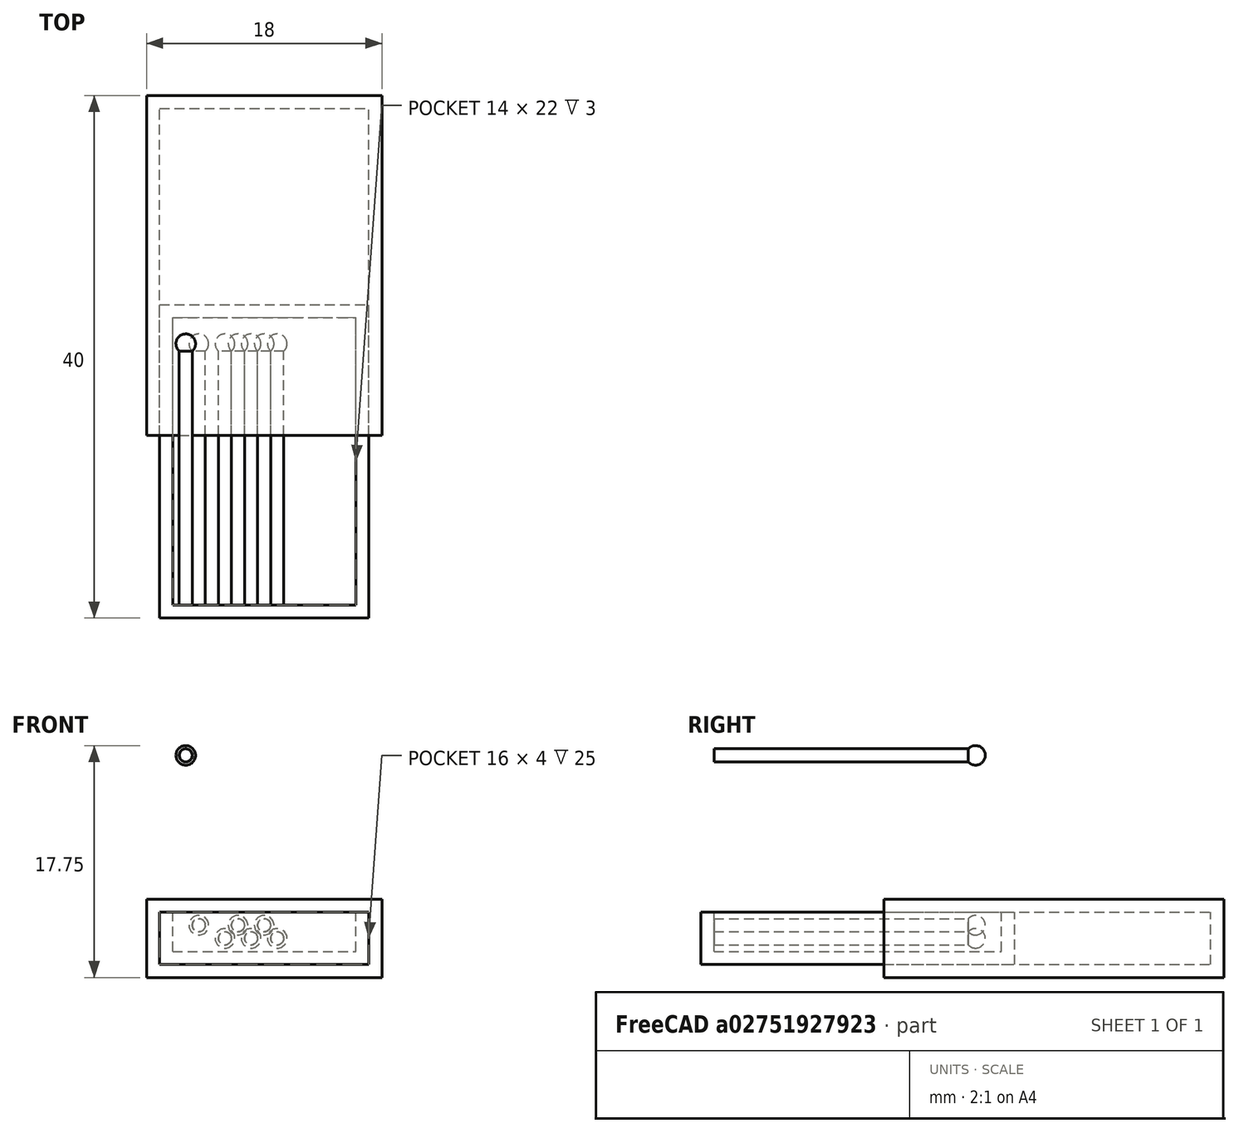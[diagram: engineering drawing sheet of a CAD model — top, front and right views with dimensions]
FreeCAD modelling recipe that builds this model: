
FCSTD DOCUMENT  (FreeCAD 0.18R4 (GitTag))
Label: 1
License: All rights reserved
LicenseURL: http://en.wikipedia.org/wiki/All_rights_reserved
objects: Part::Cylinder×7, Part::Sphere×7, Part::Fuse×7, Part::Box×4, Part::Cut×2
note: 27 computed .brp shape members not serialized (recipe doc carries the construction recipe); baked Part::Feature solids carry a one-line shape summary decoded from their .brp

FEATURE [Part::Box] Box  label="Куб"
  AttacherType = Attacher::AttachEngine3D
  Height = 4
  Length = 16
  Width = 24
FEATURE [Part::Box] Box001  label="Куб001"
  AttacherType = Attacher::AttachEngine3D
  Height = 3
  Length = 14
  Placement = pos=(1,1,1) rot=(0,0,1;0rad)
  Width = 22
FEATURE [Part::Cut] Cut
  Base = -> Box
  Tool = -> Box001
FEATURE [Part::Box] Box002  label="Куб002"
  AttacherType = Attacher::AttachEngine3D
  Height = 6
  Length = 18
  Placement = pos=(-20,2,-1) rot=(0,0,1;0rad)
  Width = 26
FEATURE [Part::Box] Box003  label="Куб003"
  AttacherType = Attacher::AttachEngine3D
  Height = 4
  Length = 16
  Placement = pos=(-19,2,0) rot=(0,0,1;0rad)
  Width = 25
FEATURE [Part::Cut] Cut001
  Base = -> Box002
  Placement = pos=(19,12,0) rot=(0,0,1;0rad)
  Tool = -> Box003
FEATURE [Part::Cylinder] Cylinder  label="Цилиндр"
  Angle = 360
  AttacherType = Attacher::AttachEngine3D
  Height = 20
  Placement = pos=(-13,1,2e-16) rot=(1,0,0;4.71239rad)
  Radius = 0.5
FEATURE [Part::Sphere] Sphere  label="Сфера"
  Angle1 = -90
  Angle2 = 90
  Angle3 = 360
  AttacherType = Attacher::AttachEngine3D
  Placement = pos=(-13,21,0) rot=(0,0,1;0rad)
  Radius = 0.75
FEATURE [Part::Fuse] Fusion
  Base = -> Cylinder
  Placement = pos=(15,0,16) rot=(0,0,1;0rad)
  Tool = -> Sphere
FEATURE [Part::Cylinder] Cylinder001  label="Цилиндр001"
  Angle = 360
  AttacherType = Attacher::AttachEngine3D
  Height = 20
  Placement = pos=(-13,1,0) rot=(-1,0,0;1.5708rad)
  Radius = 0.5
FEATURE [Part::Sphere] Sphere001  label="Сфера001"
  Angle1 = -90
  Angle2 = 90
  Angle3 = 360
  AttacherType = Attacher::AttachEngine3D
  Placement = pos=(-13,21,0) rot=(0,0,1;0rad)
  Radius = 0.75
FEATURE [Part::Fuse] Fusion001
  Base = -> Cylinder001
  Placement = pos=(16,0,3) rot=(0,0,1;0rad)
  Tool = -> Sphere001
FEATURE [Part::Cylinder] Cylinder002  label="Цилиндр002"
  Angle = 360
  AttacherType = Attacher::AttachEngine3D
  Height = 20
  Placement = pos=(-13,1,0) rot=(-1,0,0;1.5708rad)
  Radius = 0.5
FEATURE [Part::Sphere] Sphere002  label="Сфера002"
  Angle1 = -90
  Angle2 = 90
  Angle3 = 360
  AttacherType = Attacher::AttachEngine3D
  Placement = pos=(-13,21,0) rot=(0,0,1;0rad)
  Radius = 0.75
FEATURE [Part::Fuse] Fusion002
  Base = -> Cylinder002
  Placement = pos=(18,0,2) rot=(0,0,1;0rad)
  Tool = -> Sphere002
FEATURE [Part::Cylinder] Cylinder003  label="Цилиндр003"
  Angle = 360
  AttacherType = Attacher::AttachEngine3D
  Height = 20
  Placement = pos=(-13,1,0) rot=(-1,0,0;1.5708rad)
  Radius = 0.5
FEATURE [Part::Sphere] Sphere003  label="Сфера003"
  Angle1 = -90
  Angle2 = 90
  Angle3 = 360
  AttacherType = Attacher::AttachEngine3D
  Placement = pos=(-13,21,0) rot=(0,0,1;0rad)
  Radius = 0.75
FEATURE [Part::Fuse] Fusion003
  Base = -> Cylinder003
  Placement = pos=(19,0,3) rot=(0,0,1;0rad)
  Tool = -> Sphere003
FEATURE [Part::Cylinder] Cylinder004  label="Цилиндр004"
  Angle = 360
  AttacherType = Attacher::AttachEngine3D
  Height = 20
  Placement = pos=(-13,1,0) rot=(-1,0,0;1.5708rad)
  Radius = 0.5
FEATURE [Part::Sphere] Sphere004  label="Сфера004"
  Angle1 = -90
  Angle2 = 90
  Angle3 = 360
  AttacherType = Attacher::AttachEngine3D
  Placement = pos=(-13,21,0) rot=(0,0,1;0rad)
  Radius = 0.75
FEATURE [Part::Fuse] Fusion004
  Base = -> Cylinder004
  Placement = pos=(20,0,2) rot=(0,0,1;0rad)
  Tool = -> Sphere004
FEATURE [Part::Cylinder] Cylinder005  label="Цилиндр005"
  Angle = 360
  AttacherType = Attacher::AttachEngine3D
  Height = 20
  Placement = pos=(-13,1,0) rot=(-1,0,0;1.5708rad)
  Radius = 0.5
FEATURE [Part::Sphere] Sphere005  label="Сфера005"
  Angle1 = -90
  Angle2 = 90
  Angle3 = 360
  AttacherType = Attacher::AttachEngine3D
  Placement = pos=(-13,21,0) rot=(0,0,1;0rad)
  Radius = 0.75
FEATURE [Part::Fuse] Fusion005
  Base = -> Cylinder005
  Placement = pos=(21,0,3) rot=(0,0,1;0rad)
  Tool = -> Sphere005
FEATURE [Part::Cylinder] Cylinder006  label="Цилиндр006"
  Angle = 360
  AttacherType = Attacher::AttachEngine3D
  Height = 20
  Placement = pos=(-13,1,0) rot=(-1,0,0;1.5708rad)
  Radius = 0.5
FEATURE [Part::Sphere] Sphere006  label="Сфера006"
  Angle1 = -90
  Angle2 = 90
  Angle3 = 360
  AttacherType = Attacher::AttachEngine3D
  Placement = pos=(-13,21,0) rot=(0,0,1;0rad)
  Radius = 0.75
FEATURE [Part::Fuse] Fusion006
  Base = -> Cylinder006
  Placement = pos=(22,0,2) rot=(0,0,1;0rad)
  Tool = -> Sphere006
